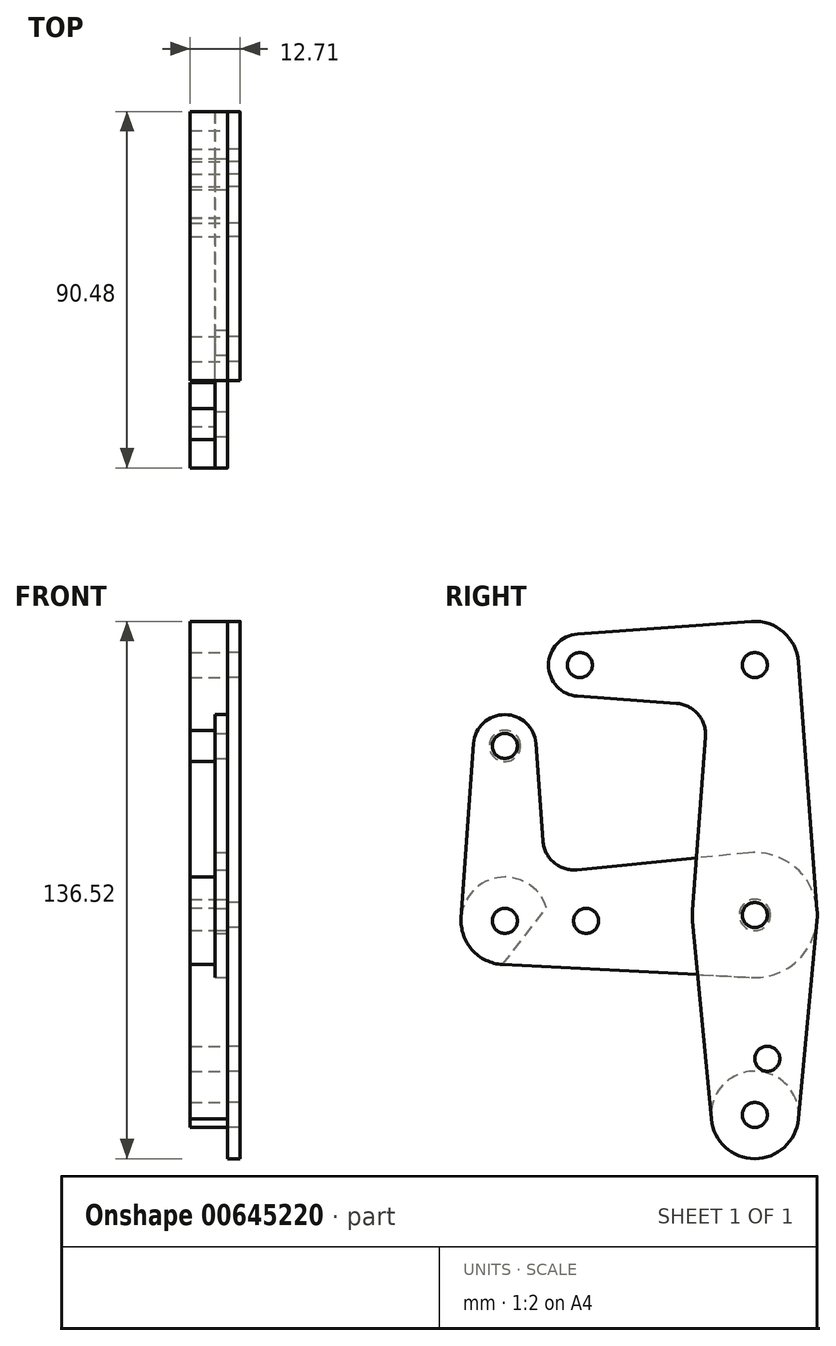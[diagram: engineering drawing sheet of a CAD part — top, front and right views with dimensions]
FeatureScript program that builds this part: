
annotation { "Feature Type Name" : "Feature", "Feature Type Description" : "" }
export const myFeature = defineFeature(function(context is Context, id is Id, definition is map)
    precondition{}
    {
        {
            var Q0;
            Q0=qCreatedBy(makeId("Right.planeOp"),FACE);
            var sketch = newSketch(context, id + "F0", { "sketchPlane" : qUnion([Q0])});
            skCircle(sketch, "E0", {"center": v(-44.45, 63.5) * mm, "radius": 7.94 * mm});
            skCircle(sketch, "E1", {"center": v(0, 63.5) * mm, "radius": 11.11 * mm});
            skCircle(sketch, "E2", {"center": v(0, 0) * mm, "radius": 15.88 * mm});
            skCircle(sketch, "E3", {"center": v(0, -50.8) * mm, "radius": 11.11 * mm});
            skCircle(sketch, "E4", {"center": v(0, -50.8) * mm, "radius": 3.18 * mm});
            skCircle(sketch, "E5", {"center": v(0, 0) * mm, "radius": 3.18 * mm});
            skCircle(sketch, "E6", {"center": v(0, 63.5) * mm, "radius": 3.18 * mm});
            skCircle(sketch, "E7", {"center": v(-44.45, 63.5) * mm, "radius": 3.18 * mm});
            skLineSegment(sketch, "E8", {"start": v(0, 0) * mm, "end": v(0, -50.8) * mm});
            skCircle(sketch, "E9", {"center": v(3.18, -36.53) * mm, "radius": 3.18 * mm});
            skLineSegment(sketch, "E10", {"start": v(-15.8, -1.49) * mm, "end": v(-11.06, -51.84) * mm});
            skLineSegment(sketch, "E11", {"start": v(11.06, -51.84) * mm, "end": v(15.8, -1.49) * mm});
            skCircle(sketch, "E12", {"center": v(0, 0) * mm, "radius": 3.98 * mm});
            skLineSegment(sketch, "E13", {"start": v(-12.52, 45.26) * mm, "end": v(-15.83, 1.2) * mm});
            skLineSegment(sketch, "E14", {"start": v(15.83, 1.2) * mm, "end": v(11.08, 64.33) * mm});
            skLineSegment(sketch, "E15", {"start": v(-45.02, 55.58) * mm, "end": v(-19.88, 53.78) * mm});
            skLineSegment(sketch, "E16", {"start": v(-45.02, 71.42) * mm, "end": v(-0.8, 74.58) * mm});
            skArc(sketch, "E17.filletArc", {"start": v(-12.52, 45.26) * mm, "mid": v(-14.43, 51.05) * mm, "end": v(-19.88, 53.78) * mm});
            skCircle(sketch, "E18", {"center": v(-63.5, -1.49) * mm, "radius": 11.11 * mm});
            skCircle(sketch, "E19", {"center": v(-63.5, 42.96) * mm, "radius": 7.94 * mm});
            skCircle(sketch, "E20", {"center": v(-42.85, -1.49) * mm, "radius": 3.18 * mm});
            skCircle(sketch, "E21", {"center": v(-63.5, -1.49) * mm, "radius": 3.18 * mm});
            skCircle(sketch, "E22", {"center": v(-63.5, 42.96) * mm, "radius": 3.18 * mm});
            skLineSegment(sketch, "E23", {"start": v(-1.56, 15.8) * mm, "end": v(-45.12, 11.5) * mm});
            skLineSegment(sketch, "E24", {"start": v(-64.07, -12.59) * mm, "end": v(-0.82, -15.85) * mm});
            skLineSegment(sketch, "E25", {"start": v(-53.83, 18.84) * mm, "end": v(-55.58, 43.52) * mm});
            skLineSegment(sketch, "E26", {"start": v(-71.42, 43.53) * mm, "end": v(-74.58, -0.7) * mm});
            skPoint(sketch, "E27.newPointB", {"position": v(-52.39, -1.49) * mm});
            skArc(sketch, "E27.filletArc", {"start": v(-53.83, 18.84) * mm, "mid": v(-51.03, 13.33) * mm, "end": v(-45.12, 11.5) * mm});
            skLineSegment(sketch, "E28", {"start": v(0, 63.5) * mm, "end": v(-44.45, 63.5) * mm, "construction": true});
            skSolve(sketch);
        }
        {
            var Q0;
            {var subQ4=sQuery(id+"F0.wireOp",EDGE,"E14");Q0=makeQuery(id+"F0.imprint","IMPRINT",FACE,{"disambiguationData":[TD([[makeQuery(id+"F0.imprint","IMPRINT",EDGE,{"derivedFrom":subQ4}),1.0]])]});}
            var Q1;
            Q1=makeQuery(id+"F0.imprint","IMPRINT",FACE,{"disambiguationData":[TD([[makeQuery(id+"F0.imprint","IMPRINT",EDGE,{"derivedFrom":sQuery(id+"F0.wireOp",EDGE,"E6")}),-1.0]])]});
            var Q2;
            Q2=makeQuery(id+"F0.imprint","IMPRINT",FACE,{"disambiguationData":[TD([[makeQuery(id+"F0.imprint","IMPRINT",EDGE,{"derivedFrom":sQuery(id+"F0.wireOp",EDGE,"E7")}),-1.0]])]});
            var Q3;
            {var subQ0=sQuery(id+"F0.wireOp",EDGE,"E10");var subQ1=sQuery(id+"F0.wireOp",EDGE,"E2");var subQ2=makeQuery(id+"F0.imprint","INTERSECT",VERTEX,{"derivedFrom":[subQ1,subQ0]});Q3=makeQuery(id+"F0.imprint","IMPRINT",FACE,{"disambiguationData":[TD([[makeQuery(id+"F0.imprint","IMPRINT",EDGE,{"disambiguationData":[TD([[subQ2,-1.0]])],"derivedFrom":subQ1}),-1.0]])]});}
            var Q4;
            {var subQ0=sQuery(id+"F0.wireOp",EDGE,"E13");var subQ1=sQuery(id+"F0.wireOp",EDGE,"E2");var subQ2=makeQuery(id+"F0.imprint","INTERSECT",VERTEX,{"derivedFrom":[subQ1,subQ0]});Q4=makeQuery(id+"F0.imprint","IMPRINT",FACE,{"disambiguationData":[TD([[makeQuery(id+"F0.imprint","IMPRINT",EDGE,{"disambiguationData":[TD([[subQ2,1.0]])],"derivedFrom":subQ1}),-1.0]])]});}
            var Q5;
            {var subQ4=sQuery(id+"F0.wireOp",EDGE,"E24");var subQ5=sQuery(id+"F0.wireOp",EDGE,"E2");var subQ6=makeQuery(id+"F0.imprint","INTERSECT",VERTEX,{"derivedFrom":[subQ5,subQ4]});Q5=makeQuery(id+"F0.imprint","IMPRINT",FACE,{"disambiguationData":[TD([[makeQuery(id+"F0.imprint","IMPRINT",EDGE,{"disambiguationData":[TD([[subQ6,-1.0]])],"derivedFrom":subQ5}),-1.0]])]});}
            var Q6;
            {var subQ3=sQuery(id+"F0.wireOp",EDGE,"E9");Q6=makeQuery(id+"F0.imprint","IMPRINT",FACE,{"disambiguationData":[TD([[makeQuery(id+"F0.imprint","IMPRINT",EDGE,{"derivedFrom":subQ3}),-1.0]])]});}
            var Q7;
            Q7=makeQuery(id+"F0.imprint","IMPRINT",FACE,{"disambiguationData":[TD([[makeQuery(id+"F0.imprint","IMPRINT",EDGE,{"derivedFrom":sQuery(id+"F0.wireOp",EDGE,"E5")}),-1.0]])]});
            var Q8;
            Q8=makeQuery(id+"F0.imprint","IMPRINT",FACE,{"disambiguationData":[TD([[makeQuery(id+"F0.imprint","IMPRINT",EDGE,{"derivedFrom":sQuery(id+"F0.wireOp",EDGE,"E12")}),-1.0]])]});
            var Q9;
            Q9=makeQuery(id+"F0.imprint","IMPRINT",FACE,{"disambiguationData":[TD([[makeQuery(id+"F0.imprint","IMPRINT",EDGE,{"derivedFrom":sQuery(id+"F0.wireOp",EDGE,"E4")}),-1.0]])]});
            extrude(context, id + "F1", {"entities" : qUnion([Q0, Q1, Q2, Q3, Q4, Q5, Q6, Q7, Q8, Q9]), "depth" : 3.17 * mm, "offsetDistance" : 25.4 * mm});
        }
        {
            var Q0;
            Q0=makeQuery(id+"F0.imprint","IMPRINT",FACE,{"disambiguationData":[TD([[makeQuery(id+"F0.imprint","IMPRINT",EDGE,{"derivedFrom":sQuery(id+"F0.wireOp",EDGE,"E12")}),-1.0]])]});
            var Q1;
            Q1=makeQuery(id+"F0.imprint","IMPRINT",FACE,{"disambiguationData":[TD([[makeQuery(id+"F0.imprint","IMPRINT",EDGE,{"derivedFrom":sQuery(id+"F0.wireOp",EDGE,"E20")}),-1.0]])]});
            var Q2;
            Q2=makeQuery(id+"F0.imprint","IMPRINT",FACE,{"disambiguationData":[TD([[makeQuery(id+"F0.imprint","IMPRINT",EDGE,{"derivedFrom":sQuery(id+"F0.wireOp",EDGE,"E21")}),-1.0]])]});
            var Q3;
            Q3=makeQuery(id+"F0.imprint","IMPRINT",FACE,{"disambiguationData":[TD([[makeQuery(id+"F0.imprint","IMPRINT",EDGE,{"derivedFrom":sQuery(id+"F0.wireOp",EDGE,"E22")}),-1.0]])]});
            var Q4;
            {var subQ0=sQuery(id+"F0.wireOp",EDGE,"E10");var subQ1=sQuery(id+"F0.wireOp",EDGE,"E2");var subQ2=makeQuery(id+"F0.imprint","INTERSECT",VERTEX,{"derivedFrom":[subQ1,subQ0]});Q4=makeQuery(id+"F0.imprint","IMPRINT",FACE,{"disambiguationData":[TD([[makeQuery(id+"F0.imprint","IMPRINT",EDGE,{"disambiguationData":[TD([[subQ2,-1.0]])],"derivedFrom":subQ1}),-1.0]])]});}
            var Q5;
            {var subQ0=sQuery(id+"F0.wireOp",EDGE,"E13");var subQ1=sQuery(id+"F0.wireOp",EDGE,"E2");var subQ2=makeQuery(id+"F0.imprint","INTERSECT",VERTEX,{"derivedFrom":[subQ1,subQ0]});Q5=makeQuery(id+"F0.imprint","IMPRINT",FACE,{"disambiguationData":[TD([[makeQuery(id+"F0.imprint","IMPRINT",EDGE,{"disambiguationData":[TD([[subQ2,1.0]])],"derivedFrom":subQ1}),-1.0]])]});}
            extrude(context, id + "F2", {"entities" : qUnion([Q0, Q1, Q2, Q3, Q4, Q5]), "oppositeDirection" : true, "depth" : 3.17 * mm, "offsetDistance" : 25.4 * mm});
        }
        {
            var Q0;
            Q0=makeQuery(id+"F1.opExtrude","CAP_FACE",FACE,{"disambiguationData":[OSD([sQuery(id+"F0.wireOp",EDGE,"E0"),sQuery(id+"F0.wireOp",EDGE,"E1"),sQuery(id+"F0.wireOp",EDGE,"E2"),sQuery(id+"F0.wireOp",EDGE,"E3"),sQuery(id+"F0.wireOp",EDGE,"E4"),sQuery(id+"F0.wireOp",EDGE,"E5"),sQuery(id+"F0.wireOp",EDGE,"E6"),sQuery(id+"F0.wireOp",EDGE,"E7"),sQuery(id+"F0.wireOp",EDGE,"E9"),sQuery(id+"F0.wireOp",EDGE,"E10"),sQuery(id+"F0.wireOp",EDGE,"E11"),sQuery(id+"F0.wireOp",EDGE,"E13"),sQuery(id+"F0.wireOp",EDGE,"E14"),sQuery(id+"F0.wireOp",EDGE,"E15"),sQuery(id+"F0.wireOp",EDGE,"E16"),sQuery(id+"F0.wireOp",EDGE,"E17.filletArc")])],"isStart":true});
            var sketch = newSketch(context, id + "F3", { "sketchPlane" : qUnion([Q0])});
            skCircle(sketch, "E29", {"center": v(0, -50.8) * mm, "radius": 11.11 * mm});
            skCircle(sketch, "E30", {"center": v(0, 0) * mm, "radius": 3.98 * mm});
            skCircle(sketch, "E31", {"center": v(0, 63.5) * mm, "radius": 3.98 * mm});
            skSolve(sketch);
        }
        {
            var Q0;
            Q0=makeQuery(id+"F2.opExtrude","CAP_FACE",FACE,{"disambiguationData":[OSD([sQuery(id+"F0.wireOp",EDGE,"E2"),sQuery(id+"F0.wireOp",EDGE,"E12"),sQuery(id+"F0.wireOp",EDGE,"E18"),sQuery(id+"F0.wireOp",EDGE,"E19"),sQuery(id+"F0.wireOp",EDGE,"E20"),sQuery(id+"F0.wireOp",EDGE,"E21"),sQuery(id+"F0.wireOp",EDGE,"E22"),sQuery(id+"F0.wireOp",EDGE,"E23"),sQuery(id+"F0.wireOp",EDGE,"E24"),sQuery(id+"F0.wireOp",EDGE,"E25"),sQuery(id+"F0.wireOp",EDGE,"E26"),sQuery(id+"F0.wireOp",EDGE,"E27.filletArc")])],"isStart":false});
            var sketch = newSketch(context, id + "F4", { "sketchPlane" : qUnion([Q0])});
            skCircle(sketch, "E32", {"center": v(63.5, -1.49) * mm, "radius": 11.11 * mm});
            skCircle(sketch, "E33", {"center": v(63.5, 42.96) * mm, "radius": 3.98 * mm});
            skCircle(sketch, "E34.0", {"center": v(0, -50.8) * mm, "radius": 3.18 * mm});
            skLineSegment(sketch, "E35", {"start": v(64.08, -12.59) * mm, "end": v(52.9, 1.82) * mm});
            skLineSegment(sketch, "E36", {"start": v(0, -50.8) * mm, "end": v(58.48, -5.38) * mm, "construction": true});
            skSolve(sketch);
        }
        {
            var Q0;
            Q0=makeQuery(id+"F1.opExtrude","CAP_FACE",FACE,{"disambiguationData":[OSD([sQuery(id+"F0.wireOp",EDGE,"E0"),sQuery(id+"F0.wireOp",EDGE,"E1"),sQuery(id+"F0.wireOp",EDGE,"E2"),sQuery(id+"F0.wireOp",EDGE,"E3"),sQuery(id+"F0.wireOp",EDGE,"E4"),sQuery(id+"F0.wireOp",EDGE,"E5"),sQuery(id+"F0.wireOp",EDGE,"E6"),sQuery(id+"F0.wireOp",EDGE,"E7"),sQuery(id+"F0.wireOp",EDGE,"E9"),sQuery(id+"F0.wireOp",EDGE,"E10"),sQuery(id+"F0.wireOp",EDGE,"E11"),sQuery(id+"F0.wireOp",EDGE,"E13"),sQuery(id+"F0.wireOp",EDGE,"E14"),sQuery(id+"F0.wireOp",EDGE,"E15"),sQuery(id+"F0.wireOp",EDGE,"E16"),sQuery(id+"F0.wireOp",EDGE,"E17.filletArc")])],"isStart":true});
            cPlane(context, id + "F5", {"entities" : qUnion([Q0]), "cplaneType" : CPlaneType.OFFSET, "offset" : 9.52 * mm, "width" : 152.4 * mm, "height" : 152.4 * mm});
        }
        {
            var Q0;
            {var subQ0=sQuery(id+"F3.wireOp",EDGE,"E29");Q0=makeQuery(id+"F3.imprint","IMPRINT",FACE,{"disambiguationData":[TD([[makeQuery(id+"F3.imprint","IMPRINT",EDGE,{"disambiguationData":[OD(0.0)],"derivedFrom":subQ0}),-1.0]])]});}
            var Q1;
            Q1=makeQuery(id+"F3.imprint","IMPRINT",FACE,{"disambiguationData":[TD([[makeQuery(id+"F3.imprint","IMPRINT",EDGE,{"derivedFrom":makeQuery(id+"F1.opExtrude","CAP_EDGE",EDGE,{"disambiguationData":[OSD([sQuery(id+"F0.wireOp",EDGE,"E4")])],"isStart":true})}),-1.0]])]});
            var Q2;
            {var subQ2=sQuery(id+"F4.wireOp",EDGE,"E35");Q2=makeQuery(id+"F4.imprint","IMPRINT",FACE,{"disambiguationData":[TD([[makeQuery(id+"F4.imprint","IMPRINT",EDGE,{"derivedFrom":subQ2}),-1.0]])]});}
            var Q3;
            Q3=makeQuery(id+"F4.imprint","IMPRINT",FACE,{"disambiguationData":[TD([[makeQuery(id+"F4.imprint","IMPRINT",EDGE,{"derivedFrom":makeQuery(id+"F2.opExtrude","CAP_EDGE",EDGE,{"disambiguationData":[OSD([sQuery(id+"F0.wireOp",EDGE,"E21")])],"isStart":true})}),1.0]])]});
            var Q4;
            Q4=makeQuery(id+"F4.imprint","IMPRINT",FACE,{"disambiguationData":[TD([[makeQuery(id+"F4.imprint","IMPRINT",EDGE,{"derivedFrom":sQuery(id+"F4.wireOp",EDGE,"E33")}),1.0]])]});
            var Q5;
            Q5=makeQuery(id+"F4.imprint","IMPRINT",FACE,{"disambiguationData":[TD([[makeQuery(id+"F4.imprint","IMPRINT",EDGE,{"derivedFrom":makeQuery(id+"F2.opExtrude","CAP_EDGE",EDGE,{"disambiguationData":[OSD([sQuery(id+"F0.wireOp",EDGE,"E22")])],"isStart":true})}),1.0]])]});
            var Q6;
            Q6=makeQuery(id+"F3.imprint","IMPRINT",FACE,{"disambiguationData":[TD([[makeQuery(id+"F3.imprint","IMPRINT",EDGE,{"derivedFrom":sQuery(id+"F3.wireOp",EDGE,"E31")}),1.0]])]});
            var Q7;
            Q7=makeQuery(id+"F3.imprint","IMPRINT",FACE,{"disambiguationData":[TD([[makeQuery(id+"F3.imprint","IMPRINT",EDGE,{"derivedFrom":makeQuery(id+"F1.opExtrude","CAP_EDGE",EDGE,{"disambiguationData":[OSD([sQuery(id+"F0.wireOp",EDGE,"E6")])],"isStart":true})}),-1.0]])]});
            var Q8;
            Q8=makeQuery(id+"F4.imprint","IMPRINT",FACE,{"disambiguationData":[TD([[makeQuery(id+"F4.imprint","IMPRINT",EDGE,{"derivedFrom":makeQuery(id+"F2.opExtrude","CAP_EDGE",EDGE,{"disambiguationData":[OSD([sQuery(id+"F0.wireOp",EDGE,"E21")])],"isStart":false})}),-1.0]])]});
            var Q9;
            Q9=makeQuery(id+"F4.imprint","IMPRINT",FACE,{"disambiguationData":[TD([[makeQuery(id+"F4.imprint","IMPRINT",EDGE,{"derivedFrom":makeQuery(id+"F2.opExtrude","CAP_EDGE",EDGE,{"disambiguationData":[OSD([sQuery(id+"F0.wireOp",EDGE,"E22")])],"isStart":false})}),-1.0]])]});
            var Q10;
            Q10=qCreatedBy(id+"F5.planeOp",FACE);
            extrude(context, id + "F6", {"entities" : qUnion([Q0, Q1, Q2, Q3, Q4, Q5, Q6, Q7, Q8, Q9]), "endBound" : BoundingType.UP_TO_SURFACE, "depth" : 25.4 * mm, "endBoundEntityFace" : qUnion([Q10]), "offsetDistance" : 25.4 * mm});
        }
    });
